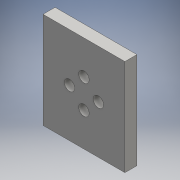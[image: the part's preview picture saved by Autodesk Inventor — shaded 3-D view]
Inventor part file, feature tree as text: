
AUTODESK INVENTOR PART (.ipt)
format: ipt  version: 2016 (Build 200138000, 138)  size: 123,392 bytes
history: native  units: mm
features: sketch x3, extrude x2, hole x1
ambient origin geometry x8: Origin, YZ Plane, XZ Plane, XY Plane, X Axis, Y Axis, Z Axis, Center Point
bodies: Solid1 (feature_tree)
feature tree (6):
  extrude  "Extrusion1"  Depth=40.0mm
  extrude  "Extrusion2"  Depth=3.0mm
  hole  "Hole1"  [1 undecoded]
  sketch  "Sketch1"  dims[d0=34.0mm d1=40.0mm]
  sketch  "Sketch2"  dims[d2=3.0mm d3=0.0mm d4=18.0mm]
  sketch  "Sketch4"  dims[d5=2.0mm d6=0.0mm d7=6.0mm d8=4.35mm d9=4.35mm d10=12.0mm d11=4.35mm d12=6.0mm d13=4.35mm d14=12.0mm d15=4.35mm d16=6.0mm d17=4.0mm d18=2.0mm d19=90.0deg d20=8.0mm d21=20.594885mm]
note: 1 required parameter value undecoded (feature->parameter linkage not recoverable at this tier; creation-order binding heuristic only, values carry confidence <= 0.55)
